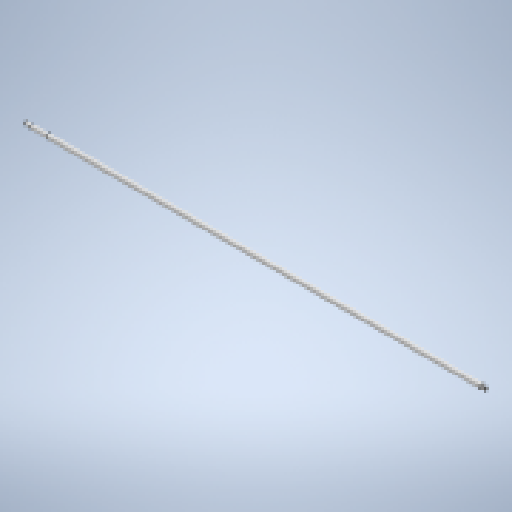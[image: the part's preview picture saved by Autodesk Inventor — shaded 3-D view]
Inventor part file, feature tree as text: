
AUTODESK INVENTOR PART (.ipt)
format: ipt  version: 2023 (Build 270158000, 158)  size: 164,352 bytes
history: native  units: in
note: dims shown in document units (in); Inventor stores cm internally (conversion verified against a paired STEP export)
features: revolve x1, sketch x1
ambient origin geometry x8: Origin, YZ Plane, XZ Plane, XY Plane, X Axis, Y Axis, Z Axis, Center Point
bodies: Solid1 (feature_tree)
feature tree (2):
  revolve  "Revolution1"  [1 undecoded]
  sketch  "Sketch1"  dims[d0=0.1575in d1=0.1969in d2=0.2362in d3=135.0deg d4=135.0deg d5=0.5906in d6=1.5354in d7=135.0deg d8=0.1575in d9=0.2756in d10=0.3937in d11=0.0079in d12=0.0354in d14=135.0deg d15=43.3071in d16=90.0deg]
note: 1 required parameter value undecoded (feature->parameter linkage not recoverable at this tier; creation-order binding heuristic only, values carry confidence <= 0.55)
